# Revit family: IS_Strada_K0779_BIM_GB
name_source: partatom
category: Plumbing Fixtures
revit_build: Autodesk Revit MEP 2014 (Build: 20130308_1515(x64)
units: mm (PartAtom-declared; Revit-internal decimal feet)

## types (1)
- K077901 - Strada Washbasin - 600mm - Under-countertop Washbasin - No taphole - with Overflow
    Accessories = www.idealspec.co.uk
    AreaUnits = millimeters
    Assembly Code = C1030200
    AssetType = Fixed
    BIMObjectName = ISI_IdealStandard_CounterTopWashBasins_Strada_K0779
    BarCode = 4015413031394
    Brand = Ideal Standard
    CWFU = 0
    CodePerformance = Vitreous china to BS 3402. Washbasin to BS EN 14688 & BS EN 31
    Color = White
    ConnectionType = Plumbing
    Cost = 0 $
    Default Elevation = 850 mm  [stored 2.78871 ft]
    Description = Strada 60cm under-countertop washbasin with overflow, no taphole
    DrainSize = 32 mm
    DurationUnit = year
    ExpectedLife = 30
    Features = 60cm under-countertop washbasin with overflow, no taphole
    Finish = White
    HWFU = 0
    Help = www.idealspec.co.uk/contact-us.html
    IfcExportAs = IfcSanitaryType
    IfcExportType = WASHHANDBASIN
    InstallationInstructions = www.idealspec.co.uk/resources.html
    LinearUnits = millimeters
    ManufacturerURL = www.idealspec.co.uk
    Material = Vitreous china
    Model = K077901
    ModelNumber = K077901
    ModelReference = Strada 60cm under-countertop washbasin with overflow, no taphole
    NBSDescription = Counter top wash basins
    NBSReference = 45-35-70/360
    Name = CounterTopWashBasins_Strada_K0779_IdealStandard
    NettWeight = 17 kg
    NominalDepth = 440 mm
    NominalHeight = 180 mm  [stored 0.590551 ft]
    NominalLength = 595 mm  [stored 1.9521 ft]
    NominalWidth = 595 mm  [stored 1.9521 ft]
    ProductInformation = www.idealspec.co.uk/assets/datasheet/K077901
    Shape = Sculptured
    Size = 595 x 440 x 180 mm
    Space = Internal
    URL = www.idealspec.co.uk
    Uniclass2015Code = Pr_40_20_96_18
    Uniclass2015Title = Counter top wash basins
    Uniclass2015Version = Products v1.1
    Version = 1
    VolumeUnits = Litres
    WFU = 0
    WarrantyDescription = Manufacturers Warranty
    WarrantyDurationParts = 99
    WarrantyDurationUnit = year
    WashHandBasinMounting = Under mounted
    WashHandBasinType = Hand Rinse

note: [stored X ft] marks values corroborated as IEEE doubles in the binary element streams (Revit-internal decimal feet)

## geometry (parser evidence)
native form markers: Sweep x3
no freeform markers — native parametric forms only
